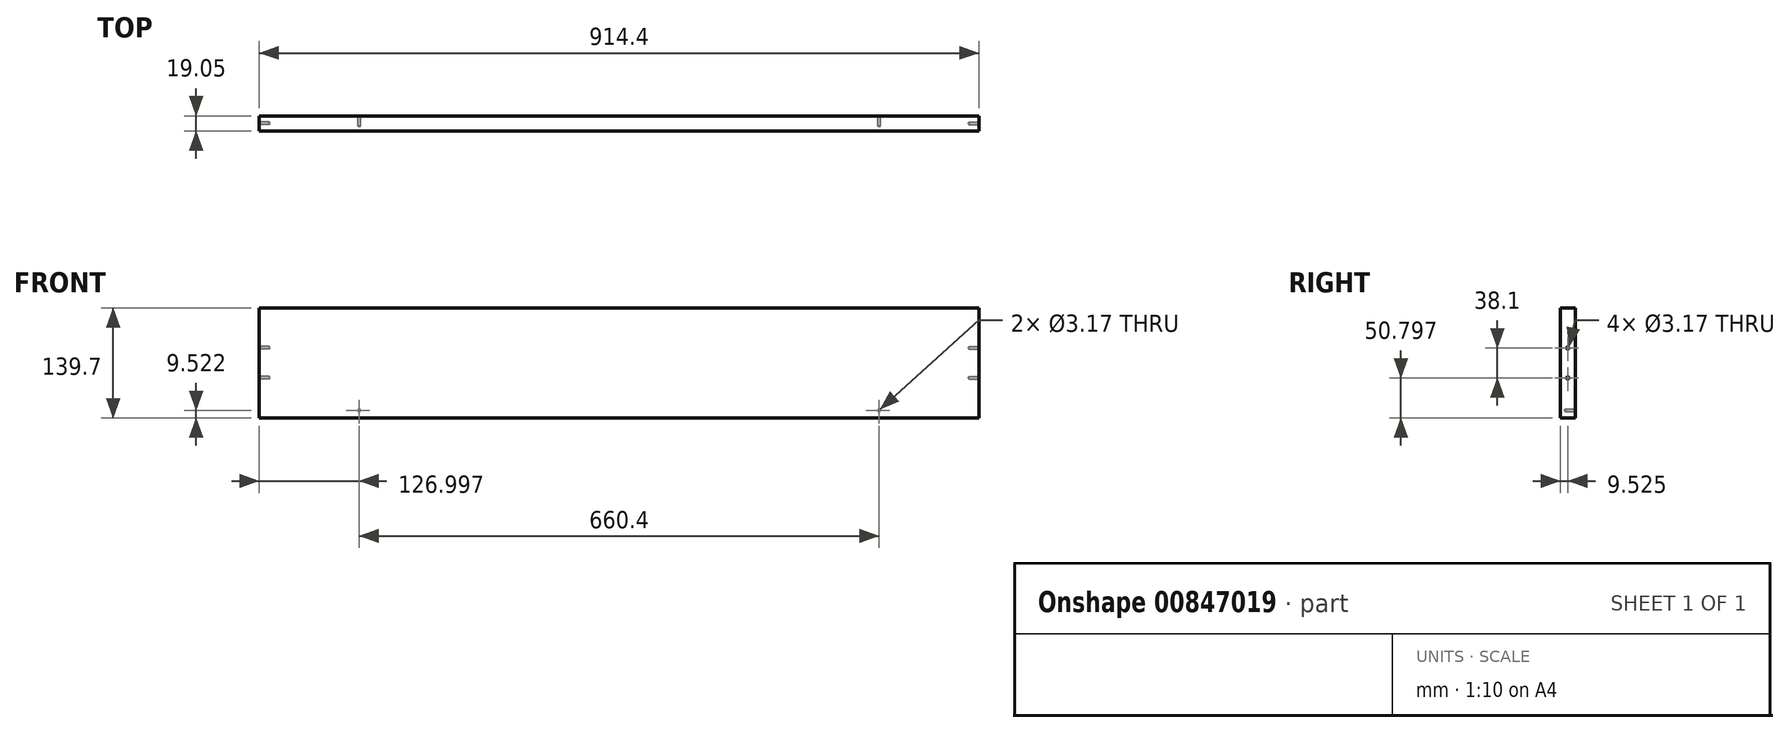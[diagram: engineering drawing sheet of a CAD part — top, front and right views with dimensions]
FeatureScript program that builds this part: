
annotation { "Feature Type Name" : "Feature", "Feature Type Description" : "" }
export const myFeature = defineFeature(function(context is Context, id is Id, definition is map)
    precondition{}
    {
        {
            var Q0;
            Q0=qCreatedBy(makeId("Front.planeOp"),FACE);
            var sketch = newSketch(context, id + "F0", { "sketchPlane" : qUnion([Q0])});
            skLineSegment(sketch, "E0.bottom", {"start": v(-193.52, 9.86) * mm, "end": v(720.88, 9.86) * mm});
            skLineSegment(sketch, "E0.top", {"start": v(-193.52, -129.84) * mm, "end": v(720.88, -129.84) * mm});
            skLineSegment(sketch, "E0.left", {"start": v(-193.52, 9.86) * mm, "end": v(-193.52, -129.84) * mm});
            skLineSegment(sketch, "E0.right", {"start": v(720.88, 9.86) * mm, "end": v(720.88, -129.84) * mm});
            skSolve(sketch);
        }
        {
            var Q0;
            Q0=makeQuery(id+"F0.imprint","IMPRINT",FACE,{"disambiguationData":[TD([[makeQuery(id+"F0.imprint","IMPRINT",EDGE,{"derivedFrom":sQuery(id+"F0.wireOp",EDGE,"E0.bottom")}),-1.0]])]});
            extrude(context, id + "F1", {"entities" : qUnion([Q0]), "depth" : 19.05 * mm, "offsetDistance" : 25.4 * mm});
        }
        {
            var Q0;
            Q0=makeQuery(id+"F1.opExtrude","SWEPT_FACE",FACE,{"disambiguationData":[OSD([sQuery(id+"F0.wireOp",EDGE,"E0.right")])]});
            var sketch = newSketch(context, id + "F2", { "sketchPlane" : qUnion([Q0])});
            skPoint(sketch, "E1", {"position": v(-9.53, -40.94) * mm});
            skPoint(sketch, "E2", {"position": v(-9.53, -79.04) * mm});
            skSolve(sketch);
        }
        {
            var Q0;
            Q0=sQuery(id+"F2.wireOp",VERTEX,"E1");
            var Q1;
            Q1=sQuery(id+"F2.wireOp",VERTEX,"E2");
            var Q2;
            Q2=makeQuery(id+"F1.opExtrude","SWEPT_BODY",BODY,{"disambiguationData":[OSD([sQuery(id+"F0.wireOp",EDGE,"E0.bottom"),sQuery(id+"F0.wireOp",EDGE,"E0.top"),sQuery(id+"F0.wireOp",EDGE,"E0.left"),sQuery(id+"F0.wireOp",EDGE,"E0.right")])]});
            hole(context, id + "F3", {"style" : HoleStyle.SIMPLE, "endStyle" : HoleEndStyle.BLIND, "holeDiameter" : 3.17 * mm, "majorDiameter" : 6.35 * mm, "holeDepth" : 12.7 * mm, "isTappedThrough" : true, "tappedDepth" : 12.7 * mm, "tapClearance" : 3, "locations" : qUnion([Q0, Q1]), "scope" : qUnion([Q2])});
        }
        {
            var Q0;
            Q0=makeQuery(id+"F1.opExtrude","SWEPT_FACE",FACE,{"disambiguationData":[OSD([sQuery(id+"F0.wireOp",EDGE,"E0.left")])]});
            var sketch = newSketch(context, id + "F4", { "sketchPlane" : qUnion([Q0])});
            skPoint(sketch, "E3", {"position": v(9.53, -40.94) * mm});
            skPoint(sketch, "E4", {"position": v(9.53, -79.04) * mm});
            skSolve(sketch);
        }
        {
            var Q0;
            Q0=sQuery(id+"F4.wireOp",VERTEX,"E3");
            var Q1;
            Q1=sQuery(id+"F4.wireOp",VERTEX,"E4");
            var Q2;
            Q2=makeQuery(id+"F1.opExtrude","SWEPT_BODY",BODY,{"disambiguationData":[OSD([sQuery(id+"F0.wireOp",EDGE,"E0.bottom"),sQuery(id+"F0.wireOp",EDGE,"E0.top"),sQuery(id+"F0.wireOp",EDGE,"E0.left"),sQuery(id+"F0.wireOp",EDGE,"E0.right")])]});
            hole(context, id + "F5", {"style" : HoleStyle.SIMPLE, "endStyle" : HoleEndStyle.BLIND, "holeDiameter" : 3.17 * mm, "majorDiameter" : 6.35 * mm, "holeDepth" : 12.7 * mm, "isTappedThrough" : true, "tappedDepth" : 12.7 * mm, "tapClearance" : 3, "locations" : qUnion([Q0, Q1]), "scope" : qUnion([Q2])});
        }
        {
            var Q0;
            Q0=makeQuery(id+"F1.opExtrude","CAP_FACE",FACE,{"disambiguationData":[OSD([sQuery(id+"F0.wireOp",EDGE,"E0.bottom"),sQuery(id+"F0.wireOp",EDGE,"E0.top"),sQuery(id+"F0.wireOp",EDGE,"E0.left"),sQuery(id+"F0.wireOp",EDGE,"E0.right")])],"isStart":true});
            var sketch = newSketch(context, id + "F6", { "sketchPlane" : qUnion([Q0])});
            skPoint(sketch, "E5", {"position": v(-593.88, -120.32) * mm});
            skPoint(sketch, "E6", {"position": v(66.52, -120.32) * mm});
            skSolve(sketch);
        }
        {
            var Q0;
            Q0=sQuery(id+"F6.wireOp",VERTEX,"E5");
            var Q1;
            Q1=sQuery(id+"F6.wireOp",VERTEX,"E6");
            var Q2;
            Q2=makeQuery(id+"F1.opExtrude","SWEPT_BODY",BODY,{"disambiguationData":[OSD([sQuery(id+"F0.wireOp",EDGE,"E0.bottom"),sQuery(id+"F0.wireOp",EDGE,"E0.top"),sQuery(id+"F0.wireOp",EDGE,"E0.left"),sQuery(id+"F0.wireOp",EDGE,"E0.right")])]});
            hole(context, id + "F7", {"style" : HoleStyle.SIMPLE, "endStyle" : HoleEndStyle.BLIND, "holeDiameter" : 3.17 * mm, "majorDiameter" : 6.35 * mm, "holeDepth" : 12.7 * mm, "isTappedThrough" : true, "tappedDepth" : 12.7 * mm, "tapClearance" : 3, "locations" : qUnion([Q0, Q1]), "scope" : qUnion([Q2])});
        }
    });
